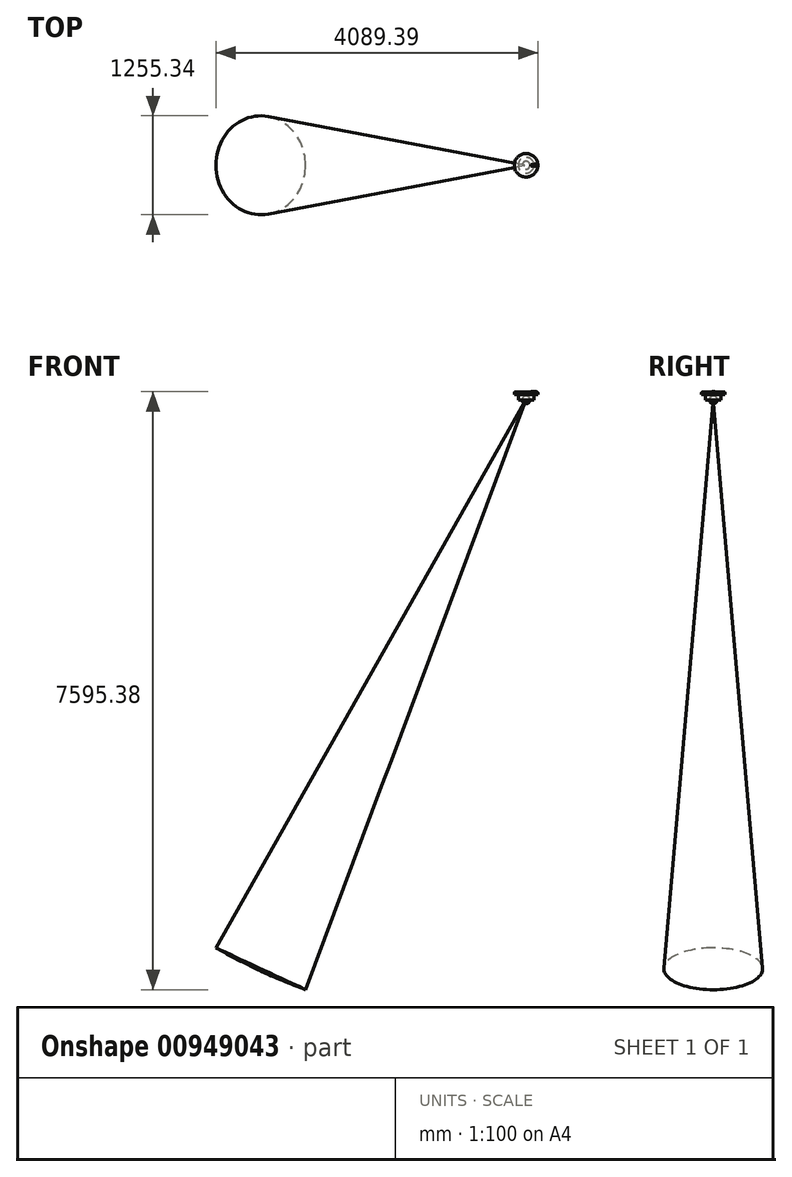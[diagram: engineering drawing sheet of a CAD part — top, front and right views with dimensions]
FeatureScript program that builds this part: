
annotation { "Feature Type Name" : "Feature", "Feature Type Description" : "" }
export const myFeature = defineFeature(function(context is Context, id is Id, definition is map)
    precondition{}
    {
        {
            var Q0;
            Q0=qCreatedBy(makeId("Front.planeOp"),FACE);
            var sketch = newSketch(context, id + "F0", { "sketchPlane" : qUnion([Q0])});
            skLineSegment(sketch, "E0", {"start": v(0, 0) * mm, "end": v(-3380.95, -7250.46) * mm});
            skLineSegment(sketch, "E1", {"start": v(0, 0) * mm, "end": v(3735.52, -1741.9) * mm, "construction": true});
            skArc(sketch, "E2", {"start": v(-3380.95, -7250.46) * mm, "mid": v(-3663, -7112.14) * mm, "end": v(-3939.39, -6962.85) * mm});
            skLineSegment(sketch, "E3", {"start": v(0, 0) * mm, "end": v(-3939.39, -6962.85) * mm});
            skLineSegment(sketch, "E4", {"start": v(-3446.96, -6092.49) * mm, "end": v(-3446.96, -6092.49) * mm});
            skLineSegment(sketch, "E5", {"start": v(0, 0) * mm, "end": v(-3446.96, -6092.49) * mm});
            skLineSegment(sketch, "E6", {"start": v(-2462.12, -4351.78) * mm, "end": v(-2462.12, -4351.78) * mm});
            skLineSegment(sketch, "E7", {"start": v(0, 0) * mm, "end": v(-2462.12, -4351.78) * mm});
            skLineSegment(sketch, "E8", {"start": v(-1969.7, -3481.42) * mm, "end": v(-1969.7, -3481.42) * mm});
            skLineSegment(sketch, "E9", {"start": v(-1969.7, -3481.42) * mm, "end": v(0, 0) * mm});
            skLineSegment(sketch, "E10", {"start": v(0, 0) * mm, "end": v(21.13, 45.32) * mm});
            skArc(sketch, "E11", {"start": v(-24.62, -43.52) * mm, "mid": v(-44.45, 22.9) * mm, "end": v(21.13, 45.32) * mm});
            skSolve(sketch);
        }
        {
            var Q0;
            {var subQ0=sQuery(id+"F0.wireOp",EDGE,"E0");Q0=makeQuery(id+"F0.imprint","IMPRINT",FACE,{"disambiguationData":[TD([[makeQuery(id+"F0.imprint","IMPRINT",EDGE,{"derivedFrom":subQ0}),-1.0]])]});}
            var Q1;
            {var subQ3=sQuery(id+"F0.wireOp",EDGE,"E4");Q1=makeQuery(id+"F0.imprint","IMPRINT",FACE,{"disambiguationData":[TD([[makeQuery(id+"F0.imprint","IMPRINT",EDGE,{"derivedFrom":subQ3}),-1.0]])]});}
            var Q2;
            {var subQ3=sQuery(id+"F0.wireOp",EDGE,"E6");Q2=makeQuery(id+"F0.imprint","IMPRINT",FACE,{"disambiguationData":[TD([[makeQuery(id+"F0.imprint","IMPRINT",EDGE,{"derivedFrom":subQ3}),-1.0]])]});}
            var Q3;
            {var subQ2=sQuery(id+"F0.wireOp",EDGE,"E8");Q3=makeQuery(id+"F0.imprint","IMPRINT",FACE,{"disambiguationData":[TD([[makeQuery(id+"F0.imprint","IMPRINT",EDGE,{"derivedFrom":subQ2}),-1.0]])]});}
            var Q4;
            {var subQ0=sQuery(id+"F0.wireOp",EDGE,"E10");Q4=makeQuery(id+"F0.imprint","IMPRINT",FACE,{"disambiguationData":[TD([[makeQuery(id+"F0.imprint","IMPRINT",EDGE,{"derivedFrom":subQ0}),1.0]])]});}
            var Q5;
            Q5=sQuery(id+"F0.wireOp",EDGE,"wBCebrRF-5z0B-UqFc-PuNl-3cCF6nvqj5QM");
            var Q6;
            Q6=sQuery(id+"F0.wireOp",EDGE,"YhsnKgyb-YJIQ-wqc7-tHqR-VzKz9Qj5qdoP");
            var Q7;
            Q7=sQuery(id+"F0.wireOp",EDGE,"E0");
            revolve(context, id + "F1", {"surfaceOperationType" : NewSurfaceOperationType.NEW, "entities" : qUnion([Q0, Q1, Q2, Q3, Q4]), "surfaceEntities" : qUnion([Q5, Q6]), "axis" : qUnion([Q7]), "revolveType" : RevolveType.FULL});
        }
        {
            var Q0;
            Q0=qCreatedBy(makeId("Right.planeOp"),FACE);
            var sketch = newSketch(context, id + "F2", { "sketchPlane" : qUnion([Q0])});
            skLineSegment(sketch, "E12.bottom", {"start": v(0, 0) * mm, "end": v(-100, 0) * mm});
            skLineSegment(sketch, "E12.top", {"start": v(0, 70) * mm, "end": v(-100, 70) * mm});
            skLineSegment(sketch, "E12.left", {"start": v(0, 0) * mm, "end": v(0, 70) * mm});
            skLineSegment(sketch, "E12.right", {"start": v(-100, 0) * mm, "end": v(-100, 70) * mm});
            skLineSegment(sketch, "E13.bottom", {"start": v(0, 70) * mm, "end": v(-150, 70) * mm});
            skLineSegment(sketch, "E13.top", {"start": v(0, 100) * mm, "end": v(-150, 100) * mm});
            skLineSegment(sketch, "E13.left", {"start": v(0, 70) * mm, "end": v(0, 100) * mm});
            skLineSegment(sketch, "E13.right", {"start": v(-150, 70) * mm, "end": v(-150, 100) * mm});
            skSolve(sketch);
        }
        {
            var Q0;
            Q0=makeQuery(id+"F2.imprint","IMPRINT",FACE,{"disambiguationData":[TD([[makeQuery(id+"F2.imprint","IMPRINT",EDGE,{"derivedFrom":sQuery(id+"F2.wireOp",EDGE,"E12.bottom")}),-1.0]])]});
            var Q1;
            Q1=makeQuery(id+"F2.imprint","IMPRINT",FACE,{"disambiguationData":[TD([[makeQuery(id+"F2.imprint","IMPRINT",EDGE,{"derivedFrom":sQuery(id+"F2.wireOp",EDGE,"E12.top")}),-1.0]])]});
            var Q2;
            Q2=sQuery(id+"F2.wireOp",EDGE,"E12.left");
            revolve(context, id + "F3", {"surfaceOperationType" : NewSurfaceOperationType.NEW, "entities" : qUnion([Q0, Q1]), "axis" : qUnion([Q2]), "revolveType" : RevolveType.FULL});
        }
        {
            var Q0;
            Q0=makeQuery(id+"F3.opRevolve","SWEPT_EDGE",EDGE,{"disambiguationData":[OSD([sQuery(id+"F2.wireOp",EDGE,"E13.top"),sQuery(id+"F2.wireOp",EDGE,"E13.right")])]});
            fillet(context, id + "F4", {"entities" : qUnion([Q0]), "radius" : 15 * mm, "tangentPropagation" : true, "allowEdgeOverflow" : false});
        }
        {
            var Q0;
            Q0=makeQuery(id+"F3.opRevolve","SWEPT_FACE",FACE,{"disambiguationData":[OSD([sQuery(id+"F2.wireOp",EDGE,"E13.top")])]});
            cPlane(context, id + "F5", {"entities" : qUnion([Q0]), "cplaneType" : CPlaneType.OFFSET, "offset" : 0 * mm, "width" : 150 * mm, "height" : 150 * mm});
        }
        {
            var Q0;
            Q0=qCreatedBy(id+"F5.planeOp",FACE);
            var sketch = newSketch(context, id + "F6", { "sketchPlane" : qUnion([Q0])});
            skLineSegment(sketch, "E14", {"start": v(132.5, 0) * mm, "end": v(102.5, 20) * mm});
            skLineSegment(sketch, "E15", {"start": v(102.5, 20) * mm, "end": v(102.5, 10) * mm});
            skLineSegment(sketch, "E16", {"start": v(102.5, 10) * mm, "end": v(62.5, 10) * mm});
            skLineSegment(sketch, "E17", {"start": v(62.5, 10) * mm, "end": v(62.5, 0) * mm});
            skLineSegment(sketch, "E18.MirrorCS", {"start": v(62.5, -10) * mm, "end": v(62.5, 0) * mm});
            skLineSegment(sketch, "E19.MirrorCS", {"start": v(102.5, -10) * mm, "end": v(62.5, -10) * mm});
            skLineSegment(sketch, "E20.MirrorCS", {"start": v(102.5, -20) * mm, "end": v(102.5, -10) * mm});
            skLineSegment(sketch, "E21.MirrorCS", {"start": v(132.5, 0) * mm, "end": v(102.5, -20) * mm});
            skSolve(sketch);
        }
        {
            var Q0;
            Q0=makeQuery(id+"F6.imprint","IMPRINT",FACE,{"disambiguationData":[TD([[makeQuery(id+"F6.imprint","IMPRINT",EDGE,{"derivedFrom":sQuery(id+"F6.wireOp",EDGE,"IaSbbVKl-1uM0-s79w-5fTL-6j28azKr0iBO")}),1.0]])]});
            var Q1;
            Q1=makeQuery(id+"F6.imprint","IMPRINT",FACE,{"disambiguationData":[TD([[makeQuery(id+"F6.imprint","IMPRINT",EDGE,{"derivedFrom":sQuery(id+"F6.wireOp",EDGE,"E14")}),1.0]])]});
            extrude(context, id + "F7", {"entities" : qUnion([Q0, Q1]), "depth" : 2 * mm, "offsetDistance" : 25 * mm});
        }
    });
